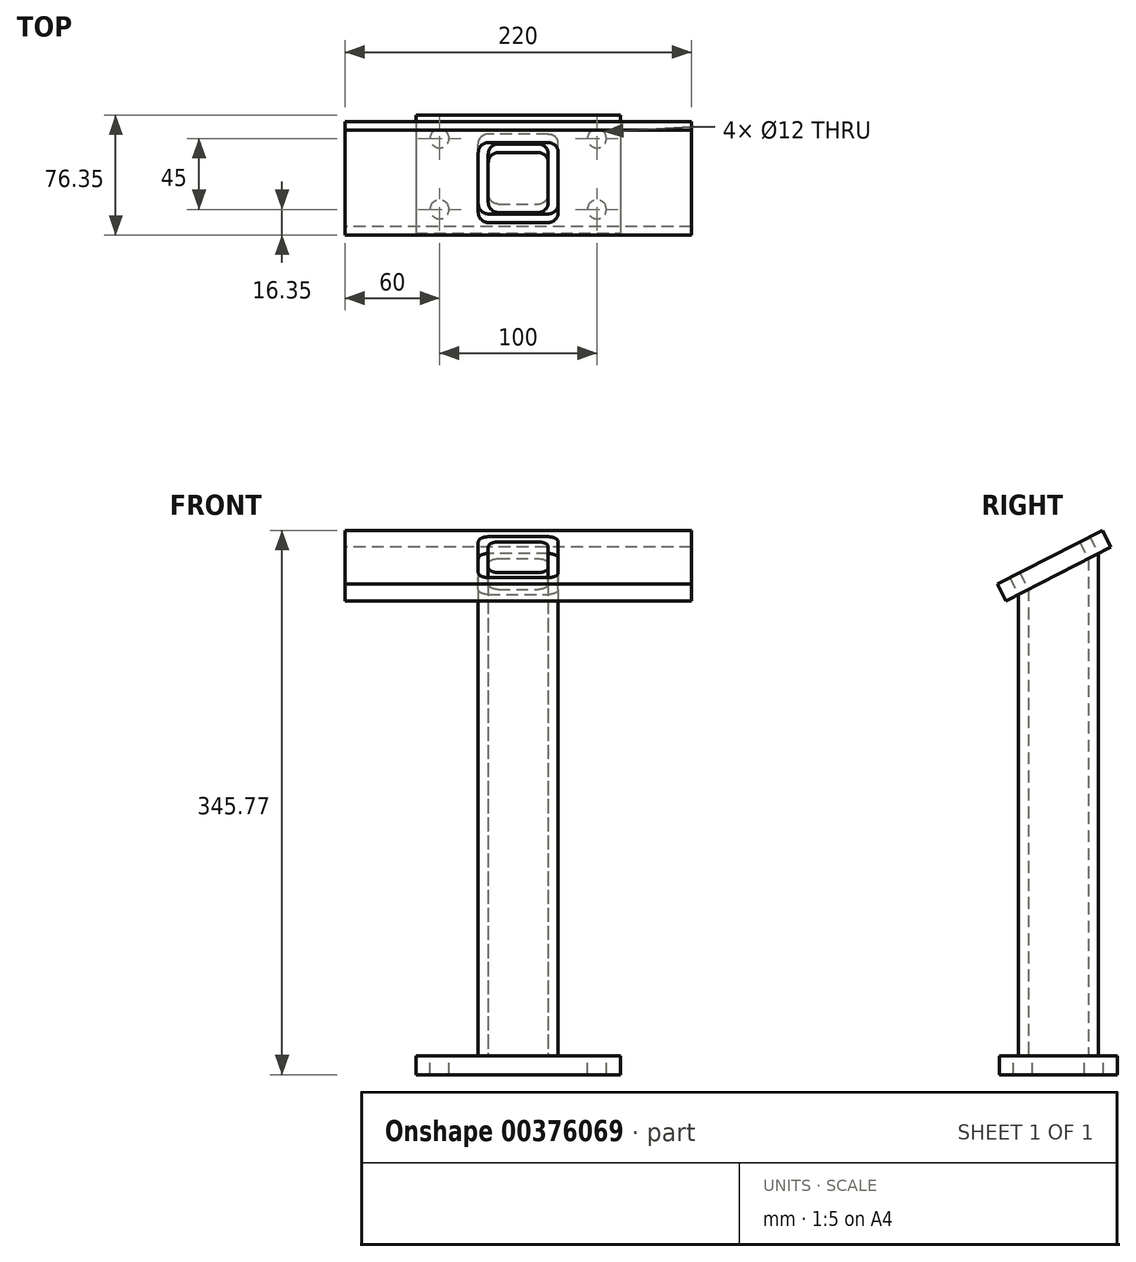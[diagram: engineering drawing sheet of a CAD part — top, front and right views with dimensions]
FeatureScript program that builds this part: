
annotation { "Feature Type Name" : "Feature", "Feature Type Description" : "" }
export const myFeature = defineFeature(function(context is Context, id is Id, definition is map)
    precondition{}
    {
        {
            var Q0;
            Q0=qCreatedBy(makeId("Top.planeOp"),FACE);
            var sketch = newSketch(context, id + "F0", { "sketchPlane" : qUnion([Q0])});
            skLineSegment(sketch, "E0.bottom", {"start": v(0, 0) * mm, "end": v(130, 0) * mm});
            skLineSegment(sketch, "E0.top", {"start": v(0, -75) * mm, "end": v(130, -75) * mm});
            skLineSegment(sketch, "E0.left", {"start": v(0, 0) * mm, "end": v(0, -75) * mm});
            skLineSegment(sketch, "E0.right", {"start": v(130, 0) * mm, "end": v(130, -75) * mm});
            skSolve(sketch);
        }
        {
            var Q0;
            Q0=makeQuery(id+"F0.imprint","IMPRINT",FACE,{"disambiguationData":[TD([[makeQuery(id+"F0.imprint","IMPRINT",EDGE,{"derivedFrom":sQuery(id+"F0.wireOp",EDGE,"E0.bottom")}),-1.0]])]});
            extrude(context, id + "F1", {"entities" : qUnion([Q0]), "depth" : 12 * mm});
        }
        {
            var Q0;
            Q0=makeQuery(id+"F1.opExtrude","CAP_FACE",FACE,{"disambiguationData":[OSD([sQuery(id+"F0.wireOp",EDGE,"E0.bottom"),sQuery(id+"F0.wireOp",EDGE,"E0.top"),sQuery(id+"F0.wireOp",EDGE,"E0.left"),sQuery(id+"F0.wireOp",EDGE,"E0.right")])],"isStart":false});
            var sketch = newSketch(context, id + "F2", { "sketchPlane" : qUnion([Q0])});
            skLineSegment(sketch, "E1.bottom", {"start": v(84.05, -12.1) * mm, "end": v(45.95, -12.1) * mm});
            skLineSegment(sketch, "E1.top", {"start": v(84.05, -62.9) * mm, "end": v(45.95, -62.9) * mm});
            skLineSegment(sketch, "E1.left", {"start": v(90.4, -18.45) * mm, "end": v(90.4, -56.55) * mm});
            skLineSegment(sketch, "E1.right", {"start": v(39.6, -18.45) * mm, "end": v(39.6, -56.55) * mm});
            skPoint(sketch, "E1.middle", {"position": v(65, -37.5) * mm});
            skPoint(sketch, "E1.middle.positionSnap0", {"position": v(65, 0) * mm});
            skPoint(sketch, "E1.middle.positionSnap1", {"position": v(0, -37.5) * mm});
            skPoint(sketch, "E1.centerSnap0", {"position": v(65, 0) * mm});
            skPoint(sketch, "E1.centerSnap1", {"position": v(0, -37.5) * mm});
            skLineSegment(sketch, "E2.bottom", {"start": v(77.7, -18.45) * mm, "end": v(52.3, -18.45) * mm});
            skLineSegment(sketch, "E2.top", {"start": v(77.7, -56.55) * mm, "end": v(52.3, -56.55) * mm});
            skLineSegment(sketch, "E2.left", {"start": v(84.05, -24.8) * mm, "end": v(84.05, -50.2) * mm});
            skLineSegment(sketch, "E2.right", {"start": v(45.95, -24.8) * mm, "end": v(45.95, -50.2) * mm});
            skPoint(sketch, "E3.visualSharp", {"position": v(45.95, -18.45) * mm});
            skArc(sketch, "E3.filletArc", {"start": v(52.3, -18.45) * mm, "mid": v(47.8, -20.3) * mm, "end": v(45.95, -24.8) * mm});
            skPoint(sketch, "E4.visualSharp", {"position": v(39.6, -12.1) * mm});
            skArc(sketch, "E4.filletArc", {"start": v(45.95, -12.1) * mm, "mid": v(41.46, -13.96) * mm, "end": v(39.6, -18.45) * mm});
            skPoint(sketch, "E5.visualSharp", {"position": v(39.6, -62.9) * mm});
            skArc(sketch, "E5.filletArc", {"start": v(39.6, -56.55) * mm, "mid": v(41.46, -61.04) * mm, "end": v(45.95, -62.9) * mm});
            skArc(sketch, "E6.filletArc", {"start": v(45.95, -50.2) * mm, "mid": v(47.8, -54.7) * mm, "end": v(52.3, -56.55) * mm});
            skPoint(sketch, "E7.visualSharp", {"position": v(90.4, -62.9) * mm});
            skArc(sketch, "E7.filletArc", {"start": v(84.05, -62.9) * mm, "mid": v(88.54, -61.04) * mm, "end": v(90.4, -56.55) * mm});
            skArc(sketch, "E8.filletArc", {"start": v(77.7, -56.55) * mm, "mid": v(82.2, -54.7) * mm, "end": v(84.05, -50.2) * mm});
            skPoint(sketch, "E9.visualSharp", {"position": v(84.05, -18.45) * mm});
            skArc(sketch, "E9.filletArc", {"start": v(84.05, -24.8) * mm, "mid": v(82.2, -20.3) * mm, "end": v(77.7, -18.45) * mm});
            skPoint(sketch, "E10.visualSharp", {"position": v(90.4, -12.1) * mm});
            skArc(sketch, "E10.filletArc", {"start": v(90.4, -18.45) * mm, "mid": v(88.54, -13.96) * mm, "end": v(84.05, -12.1) * mm});
            skSolve(sketch);
        }
        {
            var Q0;
            Q0=makeQuery(id+"F2.imprint","IMPRINT",FACE,{"disambiguationData":[TD([[makeQuery(id+"F2.imprint","IMPRINT",EDGE,{"derivedFrom":sQuery(id+"F2.wireOp",EDGE,"E1.bottom")}),1.0]])]});
            extrude(context, id + "F3", {"entities" : qUnion([Q0]), "operationType" : NewBodyOperationType.ADD, "depth" : 319 * mm});
        }
        {
            var Q0;
            Q0=makeQuery(id+"F3.opExtrude","SWEPT_FACE",FACE,{"disambiguationData":[OSD([sQuery(id+"F2.wireOp",EDGE,"E1.left")])]});
            var sketch = newSketch(context, id + "F4", { "sketchPlane" : qUnion([Q0])});
            skLineSegment(sketch, "E11", {"start": v(-18.45, 331) * mm, "end": v(-12.1, 331) * mm, "construction": true});
            skLineSegment(sketch, "E12", {"start": v(-12.1, 331) * mm, "end": v(-62.9, 331) * mm});
            skLineSegment(sketch, "E13", {"start": v(-62.9, 331) * mm, "end": v(-62.9, 305) * mm});
            skLineSegment(sketch, "E14", {"start": v(-62.9, 305) * mm, "end": v(-12.1, 331) * mm});
            skSolve(sketch);
        }
        {
            var Q0;
            Q0 = qSketchRegion(id + "F4", true);
            extrude(context, id + "F5", {"entities" : qUnion([Q0]), "operationType" : NewBodyOperationType.REMOVE, "oppositeDirection" : true, "depth" : 100 * mm});
        }
        {
            var Q0;
            Q0=makeQuery(id+"F5.boolean.opBoolean","COPY",FACE,{"derivedFrom":makeQuery(id+"F5.opExtrude","SWEPT_FACE",FACE,{"disambiguationData":[OSD([sQuery(id+"F4.wireOp",EDGE,"E14")])]})});
            var sketch = newSketch(context, id + "F6", { "sketchPlane" : qUnion([Q0])});
            skLineSegment(sketch, "E15.bottom", {"start": v(175, 149) * mm, "end": v(-45, 149) * mm});
            skLineSegment(sketch, "E15.top", {"start": v(175, 74) * mm, "end": v(-45, 74) * mm});
            skLineSegment(sketch, "E15.left", {"start": v(175, 149) * mm, "end": v(175, 74) * mm});
            skLineSegment(sketch, "E15.right", {"start": v(-45, 149) * mm, "end": v(-45, 74) * mm});
            skPoint(sketch, "E15.middle", {"position": v(65, 111.5) * mm});
            skPoint(sketch, "E15.middle.positionSnap0", {"position": v(65, 132.9) * mm});
            skPoint(sketch, "E15.middle.positionSnap1", {"position": v(45.95, 111.5) * mm});
            skPoint(sketch, "E15.centerSnap0", {"position": v(65, 132.9) * mm});
            skPoint(sketch, "E15.centerSnap1", {"position": v(45.95, 111.5) * mm});
            skSolve(sketch);
        }
        {
            var Q0;
            Q0=makeQuery(id+"F6.imprint","IMPRINT",FACE,{"disambiguationData":[TD([[makeQuery(id+"F6.imprint","IMPRINT",EDGE,{"derivedFrom":sQuery(id+"F6.wireOp",EDGE,"E15.bottom")}),1.0]])]});
            var Q1;
            {var subQ0=sQuery(id+"F4.wireOp",EDGE,"E14");Q1=makeQuery(id+"F6.imprint","IMPRINT",FACE,{"disambiguationData":[TD([[makeQuery(id+"F6.imprint","IMPRINT",EDGE,{"derivedFrom":makeQuery(id+"F5.boolean.opBoolean","COPY",EDGE,{"derivedFrom":makeQuery(id+"F5.opExtrude","CAP_EDGE",EDGE,{"disambiguationData":[OSD([subQ0])],"isStart":true})})}),1.0]])]});}
            var Q2;
            {var subQ0=makeQuery(id+"F5.opExtrude","SWEPT_FACE",FACE,{"disambiguationData":[OSD([sQuery(id+"F4.wireOp",EDGE,"E14")])]});Q2=makeQuery(id+"F6.imprint","IMPRINT",FACE,{"disambiguationData":[TD([[makeQuery(id+"F6.imprint","IMPRINT",EDGE,{"derivedFrom":makeQuery(id+"F5.boolean.opBoolean","INTERSECT",EDGE,{"derivedFrom":[makeQuery(id+"F3.opExtrude","SWEPT_FACE",FACE,{"disambiguationData":[OSD([sQuery(id+"F2.wireOp",EDGE,"E2.bottom")])]}),subQ0]})}),-1.0]])]});}
            extrude(context, id + "F7", {"entities" : qUnion([Q0, Q1, Q2]), "operationType" : NewBodyOperationType.ADD, "depth" : 12 * mm});
        }
        {
            var Q0;
            Q0=makeQuery(id+"F7.opExtrude","CAP_FACE",FACE,{"disambiguationData":[OSD([sQuery(id+"F6.wireOp",EDGE,"E15.bottom"),sQuery(id+"F6.wireOp",EDGE,"E15.top"),sQuery(id+"F6.wireOp",EDGE,"E15.left"),sQuery(id+"F6.wireOp",EDGE,"E15.right")])],"isStart":false});
            var sketch = newSketch(context, id + "F8", { "sketchPlane" : qUnion([Q0])});
            skLineSegment(sketch, "E16", {"start": v(-45, 74) * mm, "end": v(-45, 89) * mm, "construction": true});
            skLineSegment(sketch, "E17", {"start": v(-45, 89) * mm, "end": v(-30, 89) * mm, "construction": true});
            skLineSegment(sketch, "E18", {"start": v(-30, 89) * mm, "end": v(30, 89) * mm, "construction": true});
            skLineSegment(sketch, "E19", {"start": v(100, 89) * mm, "end": v(160, 89) * mm, "construction": true});
            skLineSegment(sketch, "E20", {"start": v(160, 89) * mm, "end": v(175, 89) * mm, "construction": true});
            skLineSegment(sketch, "E21", {"start": v(-30, 89) * mm, "end": v(-30, 119) * mm, "construction": true});
            skLineSegment(sketch, "E22", {"start": v(-30, 119) * mm, "end": v(30, 119) * mm, "construction": true});
            skLineSegment(sketch, "E23", {"start": v(30, 119) * mm, "end": v(100, 119) * mm, "construction": true});
            skLineSegment(sketch, "E24", {"start": v(100, 119) * mm, "end": v(160, 119) * mm, "construction": true});
            skLineSegment(sketch, "E25", {"start": v(160, 119) * mm, "end": v(160, 89) * mm, "construction": true});
            skSolve(sketch);
        }
        {
            var Q0;
            Q0=sQuery(id+"F8.wireOp",VERTEX,"E18.start");
            var Q1;
            Q1=sQuery(id+"F8.wireOp",VERTEX,"gHA1LG0g-bO6f-IzAK-ne2N-gh6vGK4VVumv.start");
            var Q2;
            Q2=sQuery(id+"F8.wireOp",VERTEX,"E19.start");
            var Q3;
            Q3=sQuery(id+"F8.wireOp",VERTEX,"E20.start");
            var Q4;
            Q4=sQuery(id+"F8.wireOp",VERTEX,"E24.end");
            var Q5;
            Q5=sQuery(id+"F8.wireOp",VERTEX,"E23.end");
            var Q6;
            Q6=sQuery(id+"F8.wireOp",VERTEX,"E22.end");
            var Q7;
            Q7=sQuery(id+"F8.wireOp",VERTEX,"E21.end");
            var Q8;
            Q8=sQuery(id+"F8.wireOp",VERTEX,"E18.end");
            var Q9;
            Q9=makeQuery(id+"F1.opExtrude","SWEPT_BODY",BODY,{"disambiguationData":[OSD([sQuery(id+"F0.wireOp",EDGE,"E0.bottom"),sQuery(id+"F0.wireOp",EDGE,"E0.top"),sQuery(id+"F0.wireOp",EDGE,"E0.left"),sQuery(id+"F0.wireOp",EDGE,"E0.right")])]});
            hole(context, id + "F9", {"style" : HoleStyle.SIMPLE, "endStyle" : HoleEndStyle.BLIND, "holeDiameter" : 12 * mm, "holeDepth" : 12 * mm, "isTappedThrough" : true, "tappedDepth" : 12 * mm, "tapClearance" : 3, "locations" : qUnion([Q0, Q1, Q2, Q3, Q4, Q5, Q6, Q7, Q8]), "scope" : qUnion([Q9])});
        }
        {
            var Q0;
            {var subQ0=sQuery(id+"F0.wireOp",EDGE,"E0.left");var subQ1=sQuery(id+"F0.wireOp",EDGE,"E0.bottom");var subQ2=sQuery(id+"F0.wireOp",EDGE,"E0.right");var subQ3=sQuery(id+"F0.wireOp",EDGE,"E0.top");Q0=makeQuery(id+"F3.boolean.opBoolean","SPLIT",FACE,{"disambiguationData":[TD([makeQuery(id+"F1.opExtrude","SWEPT_FACE",FACE,{"disambiguationData":[OSD([subQ1])]})])],"derivedFrom":makeQuery(id+"F1.opExtrude","CAP_FACE",FACE,{"disambiguationData":[OSD([subQ1,subQ3,subQ0,subQ2])],"isStart":false})});}
            var sketch = newSketch(context, id + "F10", { "sketchPlane" : qUnion([Q0])});
            skLineSegment(sketch, "E26", {"start": v(130, -75) * mm, "end": v(115, -75) * mm, "construction": true});
            skLineSegment(sketch, "E27", {"start": v(115, -75) * mm, "end": v(115, -60) * mm, "construction": true});
            skLineSegment(sketch, "E28", {"start": v(130, 0) * mm, "end": v(130, -15) * mm, "construction": true});
            skLineSegment(sketch, "E29", {"start": v(130, -15) * mm, "end": v(115, -15) * mm, "construction": true});
            skLineSegment(sketch, "E30", {"start": v(65, -75) * mm, "end": v(65, 0) * mm, "construction": true});
            skLineSegment(sketch, "E31.MirrorCS", {"start": v(15, -75) * mm, "end": v(15, -60) * mm, "construction": true});
            skLineSegment(sketch, "E32.MirrorCS", {"start": v(0, -15) * mm, "end": v(15, -15) * mm, "construction": true});
            skSolve(sketch);
        }
        {
            var Q0;
            Q0=sQuery(id+"F10.wireOp",VERTEX,"E32.MirrorCS.end");
            var Q1;
            Q1=sQuery(id+"F10.wireOp",VERTEX,"E31.MirrorCS.end");
            var Q2;
            Q2=sQuery(id+"F10.wireOp",VERTEX,"E27.end");
            var Q3;
            Q3=sQuery(id+"F10.wireOp",VERTEX,"E29.end");
            var Q4;
            Q4=makeQuery(id+"F1.opExtrude","SWEPT_BODY",BODY,{"disambiguationData":[OSD([sQuery(id+"F0.wireOp",EDGE,"E0.bottom"),sQuery(id+"F0.wireOp",EDGE,"E0.top"),sQuery(id+"F0.wireOp",EDGE,"E0.left"),sQuery(id+"F0.wireOp",EDGE,"E0.right")])]});
            hole(context, id + "F11", {"style" : HoleStyle.SIMPLE, "endStyle" : HoleEndStyle.BLIND, "holeDiameter" : 12 * mm, "holeDepth" : 12 * mm, "isTappedThrough" : true, "tappedDepth" : 12 * mm, "tapClearance" : 3, "locations" : qUnion([Q0, Q1, Q2, Q3]), "scope" : qUnion([Q4])});
        }
    });
